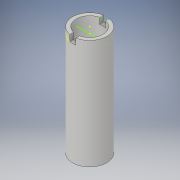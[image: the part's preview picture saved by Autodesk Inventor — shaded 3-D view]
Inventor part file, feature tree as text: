
AUTODESK INVENTOR PART (.ipt)
format: ipt  version: 2018 (Build 220112000, 112)  size: 125,440 bytes
history: native  units: in
note: dims shown in document units (in); Inventor stores cm internally (conversion verified against a paired STEP export)
features: sketch x9, extrude x3, hole x1
ambient origin geometry x8: Origin, YZ Plane, XZ Plane, XY Plane, X Axis, Y Axis, Z Axis, Center Point
bodies: Solid1 (feature_tree)
feature tree (13):
  sketch  "Sketch1"  dims[d0=0.8661in d1=1.1024in]
  extrude  "Extrusion1"  Depth=1.1024in
  hole  "Hole1"  [1 undecoded]
  extrude  "Extrusion2"  Depth=0.1969in TaperAngle=0.0deg
  sketch  "Sketch4"  dims[d15=0.1969in d16=0.0in]
  sketch  "Sketch5"
  sketch  "Sketch6"
  extrude  "Extrusion3"  [1 undecoded]
  sketch  "Sketch7"
  sketch  "Sketch8"
  sketch  "Sketch9"
  sketch  "Sketch2"  dims[d2=3.5433in d3=0.0in d4=0.3937in d5=0.3937in]
  sketch  "Sketch3"  dims[d6=0.8661in d7=0.2953in d8=0.1476in d9=0.0984in d10=90.0deg d11=3.5433in d12=0.8108in d13=0.1969in d14=0.0in]
note: 2 required parameter values undecoded (feature->parameter linkage not recoverable at this tier; creation-order binding heuristic only, values carry confidence <= 0.55)
